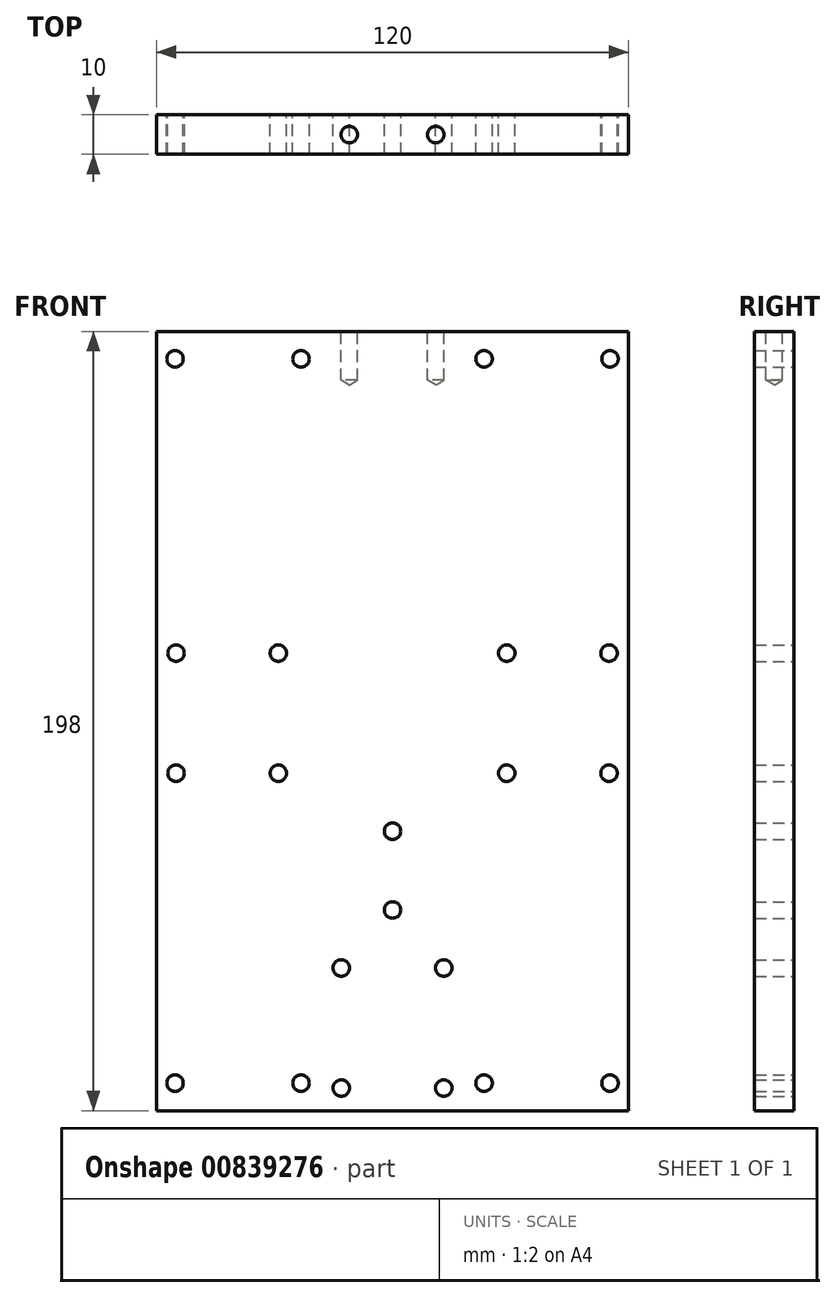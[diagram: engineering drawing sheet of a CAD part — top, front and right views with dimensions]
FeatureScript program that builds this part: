
annotation { "Feature Type Name" : "Feature", "Feature Type Description" : "" }
export const myFeature = defineFeature(function(context is Context, id is Id, definition is map)
    precondition{}
    {
        {
            var Q0;
            Q0=qCreatedBy(makeId("Front.planeOp"),FACE);
            var sketch = newSketch(context, id + "F0", { "sketchPlane" : qUnion([Q0])});
            skLineSegment(sketch, "E0.bottom", {"start": v(60, -61) * mm, "end": v(-60, -61) * mm});
            skLineSegment(sketch, "E0.top", {"start": v(60, 61) * mm, "end": v(-60, 61) * mm});
            skLineSegment(sketch, "E0.left", {"start": v(60, -61) * mm, "end": v(60, 61) * mm});
            skLineSegment(sketch, "E0.right", {"start": v(-60, -61) * mm, "end": v(-60, 61) * mm});
            skPoint(sketch, "E0.middle", {"position": v(0, 0) * mm});
            skLineSegment(sketch, "E1", {"start": v(-60, 61) * mm, "end": v(-60, 137) * mm});
            skLineSegment(sketch, "E2", {"start": v(-60, 137) * mm, "end": v(60, 137) * mm});
            skLineSegment(sketch, "E3", {"start": v(60, 137) * mm, "end": v(60, 61) * mm});
            skSolve(sketch);
        }
        {
            var Q0;
            Q0=makeQuery(id+"F0.imprint","IMPRINT",FACE,{"disambiguationData":[TD([[makeQuery(id+"F0.imprint","IMPRINT",EDGE,{"derivedFrom":sQuery(id+"F0.wireOp",EDGE,"E0.bottom")}),-1.0]])]});
            var Q1;
            Q1=makeQuery(id+"F0.imprint","IMPRINT",FACE,{"disambiguationData":[TD([[makeQuery(id+"F0.imprint","IMPRINT",EDGE,{"derivedFrom":sQuery(id+"F0.wireOp",EDGE,"E0.top")}),-1.0]])]});
            extrude(context, id + "F1", {"entities" : qUnion([Q0, Q1]), "depth" : 10 * mm, "offsetDistance" : 25 * mm});
        }
        {
            var Q0;
            Q0=makeQuery(id+"F1.opExtrude","CAP_FACE",FACE,{"disambiguationData":[OSD([sQuery(id+"F0.wireOp",EDGE,"E0.bottom"),sQuery(id+"F0.wireOp",EDGE,"E0.top"),sQuery(id+"F0.wireOp",EDGE,"E0.left"),sQuery(id+"F0.wireOp",EDGE,"E0.right")])],"isStart":true});
            var sketch = newSketch(context, id + "F2", { "sketchPlane" : qUnion([Q0])});
            skPoint(sketch, "E4", {"position": v(-55, 55.25) * mm});
            skPoint(sketch, "E5", {"position": v(-29, 55.25) * mm});
            skPoint(sketch, "E6", {"position": v(-29, 24.75) * mm});
            skPoint(sketch, "E7", {"position": v(-55, 24.75) * mm});
            skPoint(sketch, "E8.MirrorP", {"position": v(55, 55.25) * mm});
            skPoint(sketch, "E9.MirrorP", {"position": v(29, 24.75) * mm});
            skPoint(sketch, "E10.MirrorP", {"position": v(29, 55.25) * mm});
            skPoint(sketch, "E11.MirrorP", {"position": v(55, 24.75) * mm});
            skPoint(sketch, "E12", {"position": v(13, -55.25) * mm});
            skPoint(sketch, "E13", {"position": v(13, -24.75) * mm});
            skPoint(sketch, "E14.MirrorP", {"position": v(-13, -24.75) * mm});
            skPoint(sketch, "E15.MirrorP", {"position": v(-13, -55.25) * mm});
            skPoint(sketch, "E16", {"position": v(0, 10) * mm});
            skPoint(sketch, "E17.MirrorP", {"position": v(0, -10) * mm});
            skSolve(sketch);
        }
        {
            var Q0;
            Q0=sQuery(id+"F2.wireOp",VERTEX,"E4");
            var Q1;
            Q1=sQuery(id+"F2.wireOp",VERTEX,"E5");
            var Q2;
            Q2=sQuery(id+"F2.wireOp",VERTEX,"E6");
            var Q3;
            Q3=sQuery(id+"F2.wireOp",VERTEX,"E7");
            var Q4;
            Q4=sQuery(id+"F2.wireOp",VERTEX,"E10.MirrorP");
            var Q5;
            Q5=sQuery(id+"F2.wireOp",VERTEX,"E8.MirrorP");
            var Q6;
            Q6=sQuery(id+"F2.wireOp",VERTEX,"E11.MirrorP");
            var Q7;
            Q7=sQuery(id+"F2.wireOp",VERTEX,"E9.MirrorP");
            var Q8;
            Q8=sQuery(id+"F2.wireOp",VERTEX,"552e881f-070a-4ba1-a774-dd1b4211bc047.MirrorP");
            var Q9;
            Q9=sQuery(id+"F2.wireOp",VERTEX,"552e881f-070a-4ba1-a774-dd1b4211bc040.MirrorP");
            var Q10;
            Q10=sQuery(id+"F2.wireOp",VERTEX,"552e881f-070a-4ba1-a774-dd1b4211bc042.MirrorP");
            var Q11;
            Q11=sQuery(id+"F2.wireOp",VERTEX,"552e881f-070a-4ba1-a774-dd1b4211bc043.MirrorP");
            var Q12;
            Q12=sQuery(id+"F2.wireOp",VERTEX,"552e881f-070a-4ba1-a774-dd1b4211bc046.MirrorP");
            var Q13;
            Q13=sQuery(id+"F2.wireOp",VERTEX,"552e881f-070a-4ba1-a774-dd1b4211bc045.MirrorP");
            var Q14;
            Q14=sQuery(id+"F2.wireOp",VERTEX,"552e881f-070a-4ba1-a774-dd1b4211bc041.MirrorP");
            var Q15;
            Q15=sQuery(id+"F2.wireOp",VERTEX,"552e881f-070a-4ba1-a774-dd1b4211bc044.MirrorP");
            var Q16;
            Q16=sQuery(id+"F2.wireOp",VERTEX,"E14.MirrorP");
            var Q17;
            Q17=sQuery(id+"F2.wireOp",VERTEX,"E13");
            var Q18;
            Q18=sQuery(id+"F2.wireOp",VERTEX,"E12");
            var Q19;
            Q19=sQuery(id+"F2.wireOp",VERTEX,"E15.MirrorP");
            var Q20;
            Q20=sQuery(id+"F2.wireOp",VERTEX,"a8f7a37b-ae67-4c02-ba67-893163cd385e");
            var Q21;
            Q21=sQuery(id+"F2.wireOp",VERTEX,"682dddc8-d3c3-4955-9cef-4734bbbbb3d80.MirrorP");
            var Q22;
            Q22=sQuery(id+"F2.wireOp",VERTEX,"E16");
            var Q23;
            Q23=sQuery(id+"F2.wireOp",VERTEX,"E17.MirrorP");
            var Q24;
            Q24=makeQuery(id+"F1.opExtrude","SWEPT_BODY",BODY,{"disambiguationData":[OSD([sQuery(id+"F0.wireOp",EDGE,"E0.bottom"),sQuery(id+"F0.wireOp",EDGE,"E0.top"),sQuery(id+"F0.wireOp",EDGE,"E0.left"),sQuery(id+"F0.wireOp",EDGE,"E0.right")])]});
            hole(context, id + "F3", {"style" : HoleStyle.SIMPLE, "endStyle" : HoleEndStyle.THROUGH, "standardTappedOrClearance" : lookupTablePath({ "standard" : "ISO", "engagement" : "75%", "pitch" : "0.8 mm", "size" : "M5", "type" : "Tapped" }), "standardBlindInLast" : lookupTablePath({ "standard" : "ISO", "fit" : "Normal", "engagement" : "75%", "pitch" : "0.8 mm", "size" : "M5", "type" : "Clearance & tapped" }), "holeDiameter" : 4.2 * mm, "majorDiameter" : 5 * mm, "showTappedDepth" : true, "isTappedThrough" : true, "tappedDepth" : 10 * mm, "tapClearance" : 3, "locations" : qUnion([Q0, Q1, Q2, Q3, Q4, Q5, Q6, Q7, Q8, Q9, Q10, Q11, Q12, Q13, Q14, Q15, Q16, Q17, Q18, Q19, Q20, Q21, Q22, Q23]), "scope" : qUnion([Q24])});
        }
        {
            var Q0;
            Q0=makeQuery(id+"F1.opExtrude","CAP_FACE",FACE,{"disambiguationData":[OSD([sQuery(id+"F0.wireOp",EDGE,"E0.bottom"),sQuery(id+"F0.wireOp",EDGE,"E0.left"),sQuery(id+"F0.wireOp",EDGE,"E0.right"),sQuery(id+"F0.wireOp",EDGE,"E1"),sQuery(id+"F0.wireOp",EDGE,"E2"),sQuery(id+"F0.wireOp",EDGE,"E3")])],"isStart":true});
            var sketch = newSketch(context, id + "F4", { "sketchPlane" : qUnion([Q0])});
            skLineSegment(sketch, "E18", {"start": v(60, -54) * mm, "end": v(18.5, -54) * mm});
            skPoint(sketch, "E19", {"position": v(55.25, -54) * mm});
            skPoint(sketch, "E20", {"position": v(23.25, -54) * mm});
            skPoint(sketch, "E21.MirrorP", {"position": v(-23.25, -54) * mm});
            skPoint(sketch, "E22.MirrorP", {"position": v(-55.25, -54) * mm});
            skLineSegment(sketch, "E23", {"start": v(60, 38) * mm, "end": v(42.16, 38) * mm});
            skPoint(sketch, "E24.MirrorP", {"position": v(-23.25, 130) * mm});
            skPoint(sketch, "E25.MirrorP", {"position": v(-55.25, 130) * mm});
            skPoint(sketch, "E26.MirrorP", {"position": v(55.25, 130) * mm});
            skPoint(sketch, "E27.MirrorP", {"position": v(23.25, 130) * mm});
            skSolve(sketch);
        }
        {
            var Q0;
            Q0=sQuery(id+"F4.wireOp",VERTEX,"E25.MirrorP");
            var Q1;
            Q1=sQuery(id+"F4.wireOp",VERTEX,"E24.MirrorP");
            var Q2;
            Q2=sQuery(id+"F4.wireOp",VERTEX,"E27.MirrorP");
            var Q3;
            Q3=sQuery(id+"F4.wireOp",VERTEX,"E26.MirrorP");
            var Q4;
            Q4=sQuery(id+"F4.wireOp",VERTEX,"E22.MirrorP");
            var Q5;
            Q5=sQuery(id+"F4.wireOp",VERTEX,"E21.MirrorP");
            var Q6;
            Q6=sQuery(id+"F4.wireOp",VERTEX,"E20");
            var Q7;
            Q7=sQuery(id+"F4.wireOp",VERTEX,"E19");
            var Q8;
            Q8=makeQuery(id+"F1.opExtrude","SWEPT_BODY",BODY,{"disambiguationData":[OSD([sQuery(id+"F0.wireOp",EDGE,"E0.bottom"),sQuery(id+"F0.wireOp",EDGE,"E0.left"),sQuery(id+"F0.wireOp",EDGE,"E0.right"),sQuery(id+"F0.wireOp",EDGE,"E1"),sQuery(id+"F0.wireOp",EDGE,"E2"),sQuery(id+"F0.wireOp",EDGE,"E3")])]});
            hole(context, id + "F5", {"style" : HoleStyle.SIMPLE, "endStyle" : HoleEndStyle.THROUGH, "standardTappedOrClearance" : lookupTablePath({ "standard" : "ISO", "engagement" : "75%", "pitch" : "0.8 mm", "size" : "M5", "type" : "Tapped" }), "standardBlindInLast" : lookupTablePath({ "standard" : "ISO", "fit" : "Normal", "engagement" : "75%", "pitch" : "0.8 mm", "size" : "M5", "type" : "Clearance & tapped" }), "holeDiameter" : 4.2 * mm, "majorDiameter" : 5 * mm, "showTappedDepth" : true, "isTappedThrough" : true, "tappedDepth" : 10 * mm, "tapClearance" : 3, "locations" : qUnion([Q0, Q1, Q2, Q3, Q4, Q5, Q6, Q7]), "scope" : qUnion([Q8])});
        }
        {
            var Q0;
            Q0=makeQuery(id+"F1.opExtrude","SWEPT_FACE",FACE,{"disambiguationData":[OSD([sQuery(id+"F0.wireOp",EDGE,"E2")])]});
            var sketch = newSketch(context, id + "F6", { "sketchPlane" : qUnion([Q0])});
            skPoint(sketch, "E28", {"position": v(11, -5) * mm});
            skPoint(sketch, "E28.positionSnap0", {"position": v(60, -5) * mm});
            skPoint(sketch, "E29.MirrorP", {"position": v(-11, -5) * mm});
            skSolve(sketch);
        }
        {
            var Q0;
            Q0=sQuery(id+"F6.wireOp",VERTEX,"E28");
            var Q1;
            Q1=sQuery(id+"F6.wireOp",VERTEX,"E29.MirrorP");
            var Q2;
            Q2=makeQuery(id+"F1.opExtrude","SWEPT_BODY",BODY,{"disambiguationData":[OSD([sQuery(id+"F0.wireOp",EDGE,"E0.bottom"),sQuery(id+"F0.wireOp",EDGE,"E0.left"),sQuery(id+"F0.wireOp",EDGE,"E0.right"),sQuery(id+"F0.wireOp",EDGE,"E1"),sQuery(id+"F0.wireOp",EDGE,"E2"),sQuery(id+"F0.wireOp",EDGE,"E3")])]});
            hole(context, id + "F7", {"style" : HoleStyle.SIMPLE, "endStyle" : HoleEndStyle.BLIND, "standardTappedOrClearance" : lookupTablePath({ "standard" : "ISO", "engagement" : "75%", "pitch" : "0.8 mm", "size" : "M5", "type" : "Tapped" }), "standardBlindInLast" : lookupTablePath({ "standard" : "ISO", "fit" : "Normal", "engagement" : "75%", "pitch" : "0.8 mm", "size" : "M5", "type" : "Clearance & tapped" }), "holeDiameter" : 4.2 * mm, "majorDiameter" : 5 * mm, "showTappedDepth" : true, "holeDepth" : 12.4 * mm, "isTappedThrough" : true, "tappedDepth" : 10 * mm, "tapClearance" : 3, "locations" : qUnion([Q0, Q1]), "scope" : qUnion([Q2])});
        }
    });
